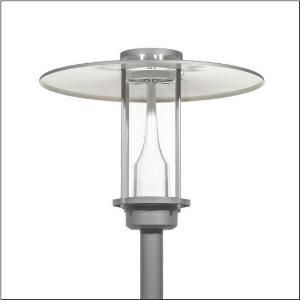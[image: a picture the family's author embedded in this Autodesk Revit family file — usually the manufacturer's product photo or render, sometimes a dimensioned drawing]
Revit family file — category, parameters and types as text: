
# Revit family: city-light_plus_iq___st1_2a_5xa5275af14hp_3410
name_source: partatom
category: Lighting Fixtures
units: mm (PartAtom-declared; Revit-internal decimal feet)

## family parameters
Cut with Voids When Loaded = No
Host = Face
Light Source = No
Part Type = Normal
Room Calculation Point = No
Round Connector Dimension = Use Diameter
Shared = No

## types (1)
- --- (1 x LED, 3730 lm, 33.6 W, 2200K)
    Apparent Load = 34 VA
    CIE Flux Codes = 22 60 93 97 100
    Color Rendering = 70
    Color Temperature = 2200K
    Default Elevation = 1800 mm
    Description = City-Light Plus iQ, mast luminaire, Module 540 iQ-SR, primary light control with 3 zone facetted reflector, of plastic, silver coated, highly specular, structured, primary optical cover: cover, of PMMA, transparent, light distribution: ST1.2a, light emission: direct distribution, primary light characteristic: asymmetric, installation type: post-top, LED, High Power LED, rated luminous flux: 3.730lm, luminous efficacy: 111lm/W, light colour: 722, colour temperature: 2200K, control gear: ECG iQ, control: presetting dimming logarithmic, Street-Remote, Auto-Match, Temp-Guard, Lumen-Switch, Night-Set, Smart-Wire, Light-Fading, Desk-Remote (wireless, voltage-free reading and setting of iQ features in the workshop via application-optimized NFC function/RFID function), optimised constant luminous flux control (CLO 2.0), with terminal, 6-pole, max. 2.5mm², mains connection: 230..240V, AC, 50/60Hz, start of lifetime: 34W, end of service life: 36W, reduction: 15W, luminaire housing, upper part, of glass-fibre reinforced polyester, coated, Siteco® metallic grey (DB 702S), diameter: 750mm, height: 590mm, spigot size: d x l = 76 x 70mm (post-top) | with reducer (optional accessory) 60 x 70mm, post-top mast mounting element, of diecast aluminium, coated, Siteco® metallic grey (DB 702S), Module 540 iQ-SR, traffic white (RAL 9016), equipment: Power, protection rating (complete): IP65, insulation class (complete): insulation class II (safety insulation), certification: CE, ENEC, VDE, packaging unit: 1 piece

Light Distribution: ST1.2a
    Height = 590 mm
    Lamp = 1 x LED
    Lamp Light Flux = 3730 lm
    Lamp Power = 33.6 W
    Lamp count = 1
    Length = 750 mm
    Luminous efficacy = 111 lm/W
    Manufacturer = Siteco
    ModVariant = No
    Model = 5XA5275AF14HP
    Number of Poles = 1
    OnlyDefault = Yes
    Power Factor = 1
    Product Name = City-Light Plus iQ | ST1.2a
    Product group = mast luminaire | pylon top
    ProductGroupID = 6100
    Protection Class = Protection class II
    Protection Degree = IP 65
    RLX_Detail_Level = 1
    RLX_Emergency_Light_Flux = 0 lm
    RLX_Emergency_Type = 0
    RLX_Emergency_Type_DB = No
    RlxData = <blob elided: 52529 chars, md5=919a590d>
    Socket = socket
    Standby Power = 0 W
    System Light Flux = 3730 lm
    System Power = 34 W
    Type Comments = factory setting: luminous flux: 100 % | dim-lin: 254 | 695 mA
    Type Image = l_1006456.jpg
    URL = http://relux.com
    VarID = @adj_146531
    Voltage = 0 V
    Weight = 0.00 kg
    Width = 0 mm  [stored 0 ft]

note: [stored X ft] marks values corroborated as IEEE doubles in the binary element streams (Revit-internal decimal feet)

## geometry (parser evidence)
native form markers: Blend x4, Sweep x12
no freeform markers — native parametric forms only
